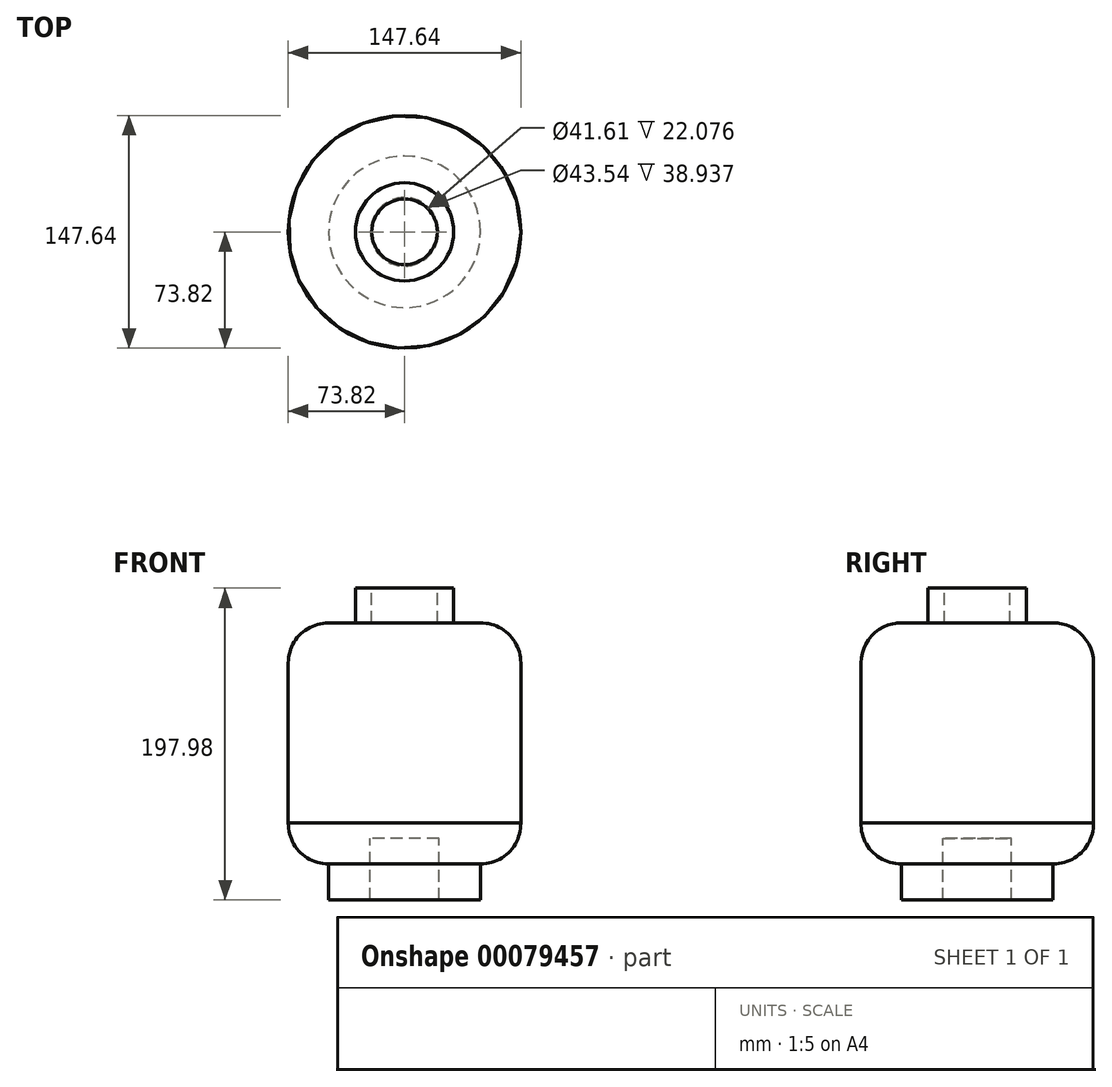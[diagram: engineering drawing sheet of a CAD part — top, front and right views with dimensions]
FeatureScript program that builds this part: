
annotation { "Feature Type Name" : "Feature", "Feature Type Description" : "" }
export const myFeature = defineFeature(function(context is Context, id is Id, definition is map)
    precondition{}
    {
        {
            var Q0;
            Q0=qCreatedBy(makeId("Front.planeOp"),FACE);
            var sketch = newSketch(context, id + "F0", { "sketchPlane" : qUnion([Q0])});
            skLineSegment(sketch, "E0", {"start": v(0, -74.47) * mm, "end": v(0, 128.73) * mm});
            skLineSegment(sketch, "E1", {"start": v(0, 55.19) * mm, "end": v(20.8, 55.19) * mm});
            skLineSegment(sketch, "E2", {"start": v(20.8, 55.19) * mm, "end": v(20.8, 77.26) * mm});
            skLineSegment(sketch, "E3", {"start": v(20.8, 77.26) * mm, "end": v(31.21, 77.26) * mm});
            skLineSegment(sketch, "E4", {"start": v(31.21, 77.26) * mm, "end": v(31.21, 55.19) * mm});
            skLineSegment(sketch, "E5", {"start": v(31.21, 55.19) * mm, "end": v(48.21, 55.19) * mm});
            skLineSegment(sketch, "E6", {"start": v(73.81, 29.79) * mm, "end": v(73.81, -71.81) * mm});
            skArc(sketch, "E7", {"start": v(73.81, 29.79) * mm, "mid": v(66.3, 47.82) * mm, "end": v(48.21, 55.19) * mm});
            skLineSegment(sketch, "E8", {"start": v(48.42, -97.86) * mm, "end": v(48.17, -97.86) * mm});
            skLineSegment(sketch, "E9", {"start": v(48.17, -97.86) * mm, "end": v(48.17, -120.72) * mm});
            skLineSegment(sketch, "E10", {"start": v(48.17, -120.72) * mm, "end": v(21.77, -120.72) * mm});
            skLineSegment(sketch, "E11", {"start": v(21.77, -120.72) * mm, "end": v(21.77, -81.78) * mm});
            skLineSegment(sketch, "E12", {"start": v(21.77, -81.78) * mm, "end": v(0, -81.78) * mm});
            skArc(sketch, "E13", {"start": v(48.42, -97.86) * mm, "mid": v(66.61, -90.19) * mm, "end": v(73.81, -71.81) * mm});
            skSolve(sketch);
        }
        {
            var Q0;
            Q0=sQuery(id+"F0.wireOp",EDGE,"E7");
            var Q1;
            Q1=sQuery(id+"F0.wireOp",EDGE,"E5");
            var Q2;
            Q2=sQuery(id+"F0.wireOp",EDGE,"E4");
            var Q3;
            Q3=sQuery(id+"F0.wireOp",EDGE,"E2");
            var Q4;
            Q4=sQuery(id+"F0.wireOp",EDGE,"E3");
            var Q5;
            Q5=sQuery(id+"F0.wireOp",EDGE,"E1");
            var Q6;
            Q6=sQuery(id+"F0.wireOp",EDGE,"E12");
            var Q7;
            Q7=sQuery(id+"F0.wireOp",EDGE,"E11");
            var Q8;
            Q8=sQuery(id+"F0.wireOp",EDGE,"E10");
            var Q9;
            Q9=sQuery(id+"F0.wireOp",EDGE,"E9");
            var Q10;
            Q10=sQuery(id+"F0.wireOp",EDGE,"E8");
            var Q11;
            Q11=sQuery(id+"F0.wireOp",EDGE,"E13");
            var Q12;
            Q12=sQuery(id+"F0.wireOp",EDGE,"E6");
            var Q13;
            Q13=sQuery(id+"F0.wireOp",EDGE,"E0");
            revolve(context, id + "F1", {"bodyType" : ToolBodyType.SURFACE, "surfaceEntities" : qUnion([Q0, Q1, Q2, Q3, Q4, Q5, Q6, Q7, Q8, Q9, Q10, Q11, Q12]), "axis" : qUnion([Q13]), "revolveType" : RevolveType.FULL});
        }
    });
